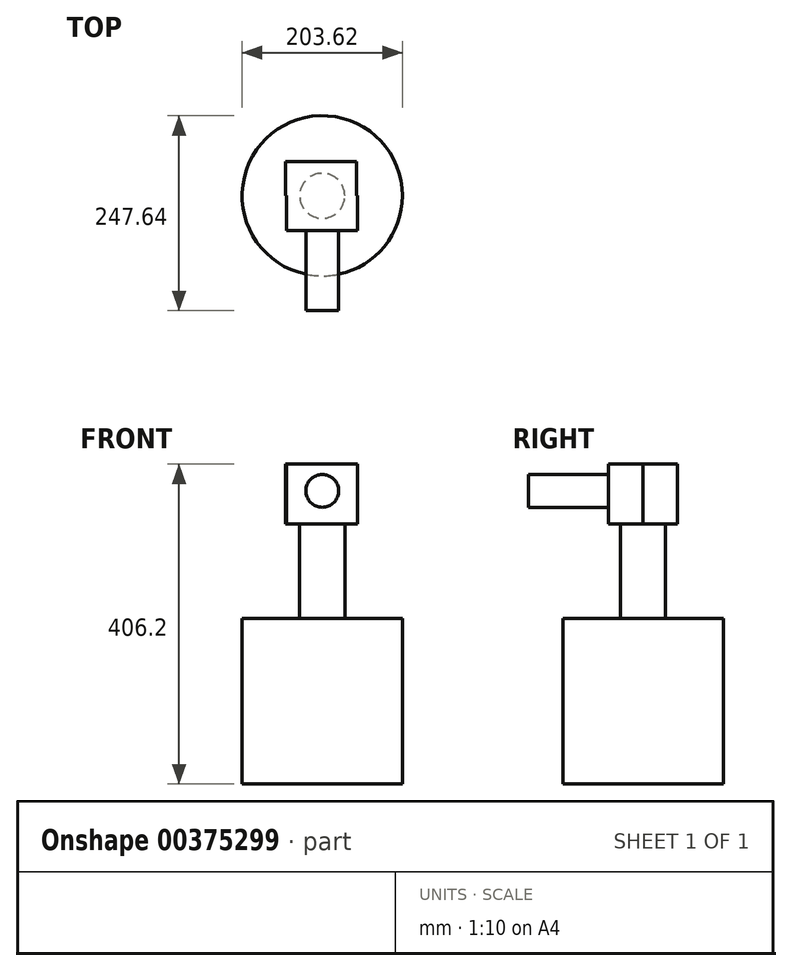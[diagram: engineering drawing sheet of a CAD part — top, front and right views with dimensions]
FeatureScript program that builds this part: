
annotation { "Feature Type Name" : "Feature", "Feature Type Description" : "" }
export const myFeature = defineFeature(function(context is Context, id is Id, definition is map)
    precondition{}
    {
        {
            var Q0;
            Q0=qCreatedBy(makeId("Top.planeOp"),FACE);
            var sketch = newSketch(context, id + "F0", { "sketchPlane" : qUnion([Q0])});
            skCircle(sketch, "E0", {"center": v(0, 0) * mm, "radius": 101.8 * mm});
            skSolve(sketch);
        }
        {
            var Q0;
            Q0=makeQuery(id+"F0.imprint","IMPRINT",FACE,{"disambiguationData":[TD([[makeQuery(id+"F0.imprint","IMPRINT",EDGE,{"derivedFrom":sQuery(id+"F0.wireOp",EDGE,"E0")}),1.0]])]});
            extrude(context, id + "F1", {"entities" : qUnion([Q0]), "depth" : 160 * mm});
        }
        {
            var Q0;
            Q0=makeQuery(id+"F1.opExtrude","CAP_FACE",FACE,{"disambiguationData":[OSD([sQuery(id+"F0.wireOp",EDGE,"E0")])],"isStart":false});
            var sketch = newSketch(context, id + "F2", { "sketchPlane" : qUnion([Q0])});
            skCircle(sketch, "E1", {"center": v(0, 0) * mm, "radius": 28.58 * mm});
            skSolve(sketch);
        }
        {
            var Q0;
            Q0=makeQuery(id+"F2.imprint","IMPRINT",FACE,{"disambiguationData":[TD([[makeQuery(id+"F2.imprint","IMPRINT",EDGE,{"derivedFrom":sQuery(id+"F2.wireOp",EDGE,"E1")}),1.0]])]});
            var Q1;
            Q1 = qSketchRegion(id + "F2", true);
            extrude(context, id + "F3", {"entities" : qUnion([Q0, Q1]), "operationType" : NewBodyOperationType.ADD, "depth" : 120 * mm});
        }
        {
            var Q0;
            Q0=makeQuery(id+"F1.opExtrude","CAP_FACE",FACE,{"disambiguationData":[OSD([sQuery(id+"F0.wireOp",EDGE,"E0")])],"isStart":true});
            extrude(context, id + "F4", {"entities" : qUnion([Q0]), "operationType" : NewBodyOperationType.ADD, "depth" : 50 * mm});
        }
        {
            var Q0;
            Q0=makeQuery(id+"F3.opExtrude","CAP_FACE",FACE,{"disambiguationData":[OSD([sQuery(id+"F2.wireOp",EDGE,"E1")])],"isStart":false});
            var sketch = newSketch(context, id + "F5", { "sketchPlane" : qUnion([Q0])});
            skCircle(sketch, "E2", {"center": v(0, 0) * mm, "radius": 36.86 * mm});
            skLineSegment(sketch, "E3", {"start": v(5.83, -36.4) * mm, "end": v(0, 36.86) * mm});
            skSolve(sketch);
        }
        {
            var Q0;
            Q0 = qSketchRegion(id + "F5", true);
            var sketch = newSketch(context, id + "F6", { "sketchPlane" : qUnion([Q0])});
            skLineSegment(sketch, "E4.bottom", {"start": v(44.7, 0) * mm, "end": v(-45.43, 0) * mm});
            skLineSegment(sketch, "E4.top", {"start": v(44.7, -44.23) * mm, "end": v(-45.43, -44.23) * mm});
            skLineSegment(sketch, "E4.left", {"start": v(44.7, 0) * mm, "end": v(44.7, -44.23) * mm});
            skLineSegment(sketch, "E4.right", {"start": v(-45.43, 0) * mm, "end": v(-45.43, -44.23) * mm});
            skSolve(sketch);
        }
        {
            var Q0;
            Q0 = qSketchRegion(id + "F5", true);
            var sketch = newSketch(context, id + "F7", { "sketchPlane" : qUnion([Q0])});
            skLineSegment(sketch, "E5.bottom", {"start": v(43.64, 0) * mm, "end": v(-46.8, 0) * mm});
            skLineSegment(sketch, "E5.top", {"start": v(43.64, 43.64) * mm, "end": v(-46.8, 43.64) * mm});
            skLineSegment(sketch, "E5.left", {"start": v(43.64, 0) * mm, "end": v(43.64, 43.64) * mm});
            skLineSegment(sketch, "E5.right", {"start": v(-46.8, 0) * mm, "end": v(-46.8, 43.64) * mm});
            skSolve(sketch);
        }
        {
            var Q0;
            Q0 = qSketchRegion(id + "F6", true);
            var Q1;
            Q1 = qSketchRegion(id + "F7", true);
            extrude(context, id + "F8", {"entities" : qUnion([Q0, Q1]), "operationType" : NewBodyOperationType.ADD, "depth" : 76.2 * mm});
        }
        {
            var Q0;
            Q0=makeQuery(id+"F8.opExtrude","SWEPT_FACE",FACE,{"disambiguationData":[OSD([sQuery(id+"F6.wireOp",EDGE,"E4.top")])]});
            var sketch = newSketch(context, id + "F9", { "sketchPlane" : qUnion([Q0])});
            skCircle(sketch, "E6", {"center": v(0, 322.2) * mm, "radius": 20.79 * mm});
            skSolve(sketch);
        }
        {
            var Q0;
            Q0=makeQuery(id+"F9.imprint","IMPRINT",FACE,{"disambiguationData":[TD([[makeQuery(id+"F9.imprint","IMPRINT",EDGE,{"derivedFrom":sQuery(id+"F9.wireOp",EDGE,"E6")}),1.0]])]});
            extrude(context, id + "F10", {"entities" : qUnion([Q0]), "operationType" : NewBodyOperationType.ADD, "depth" : 101.6 * mm});
        }
    });
